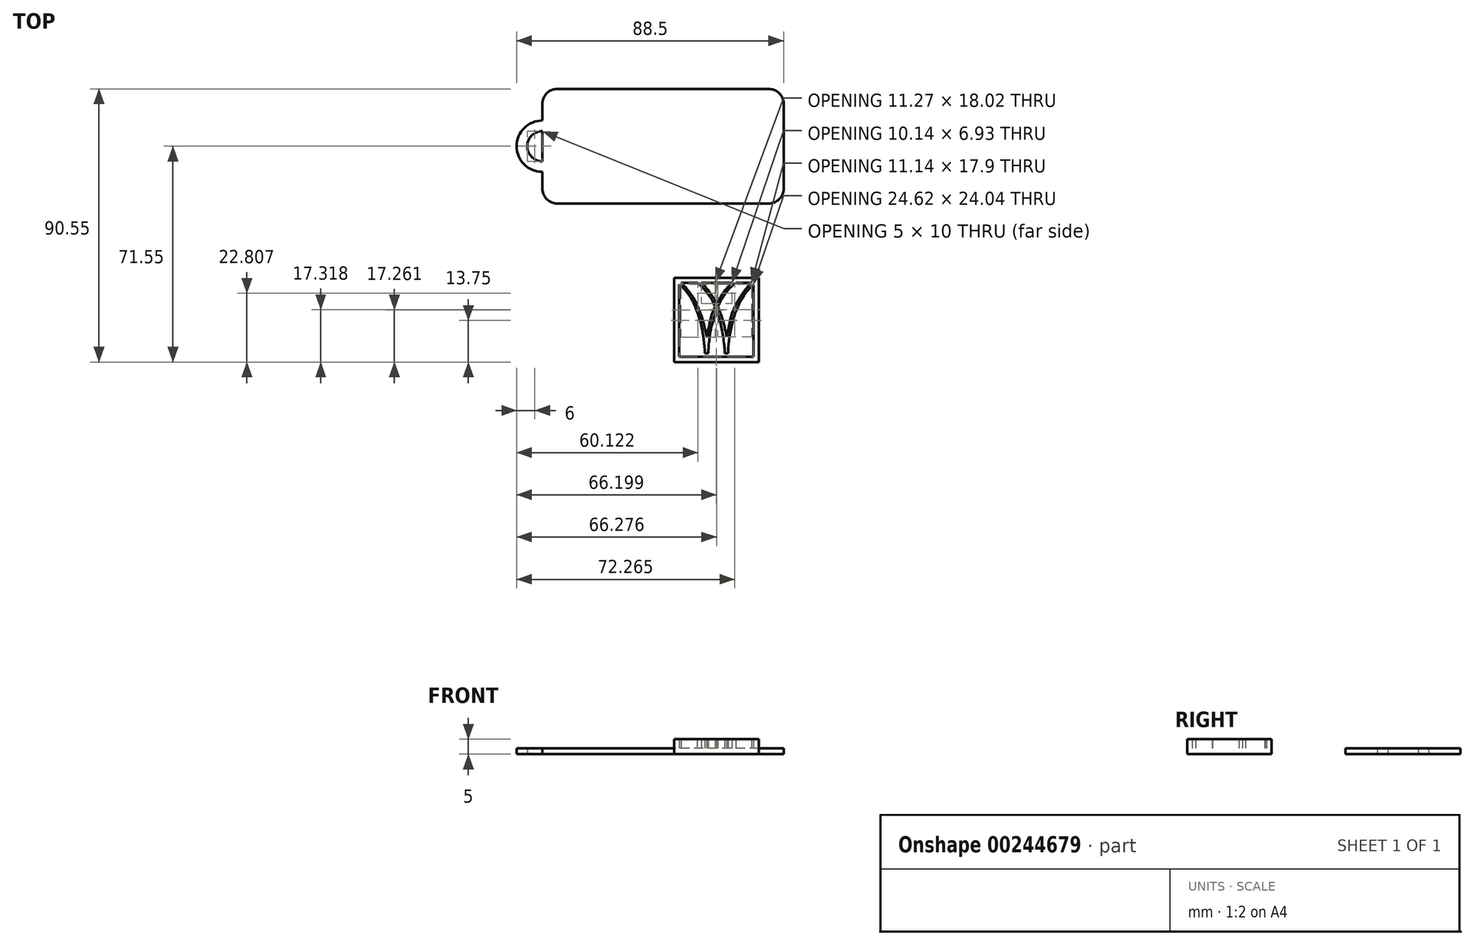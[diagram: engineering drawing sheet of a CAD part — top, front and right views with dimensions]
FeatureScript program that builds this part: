
annotation { "Feature Type Name" : "Feature", "Feature Type Description" : "" }
export const myFeature = defineFeature(function(context is Context, id is Id, definition is map)
    precondition{}
    {
        {
            var Q0;
            Q0=qCreatedBy(makeId("Top.planeOp"),FACE);
            var sketch = newSketch(context, id + "F0", { "sketchPlane" : qUnion([Q0])});
            skLineSegment(sketch, "E0.bottom", {"start": v(40, -19) * mm, "end": v(-40, -19) * mm});
            skLineSegment(sketch, "E0.top", {"start": v(40, 19) * mm, "end": v(-40, 19) * mm});
            skLineSegment(sketch, "E0.left", {"start": v(40, -19) * mm, "end": v(40, 19) * mm});
            skLineSegment(sketch, "E0.right", {"start": v(-40, -19) * mm, "end": v(-40, 19) * mm});
            skPoint(sketch, "E0.middle", {"position": v(0, 0) * mm});
            skArc(sketch, "E1", {"start": v(-40, 8.5) * mm, "mid": v(-48.5, 0) * mm, "end": v(-40, -8.5) * mm});
            skArc(sketch, "E2", {"start": v(-40, 5) * mm, "mid": v(-45, 0) * mm, "end": v(-40, -5) * mm});
            skLineSegment(sketch, "E3.bottom", {"start": v(3.67, -43.6) * mm, "end": v(31.76, -43.6) * mm});
            skLineSegment(sketch, "E3.top", {"start": v(3.67, -71.55) * mm, "end": v(31.76, -71.55) * mm});
            skLineSegment(sketch, "E3.left", {"start": v(3.67, -43.6) * mm, "end": v(3.67, -71.55) * mm});
            skLineSegment(sketch, "E3.right", {"start": v(31.76, -43.6) * mm, "end": v(31.76, -71.55) * mm});
            skLineSegment(sketch, "E4.bottom", {"start": v(30, -69.82) * mm, "end": v(5.4, -69.82) * mm});
            skLineSegment(sketch, "E4.top", {"start": v(30, -45.28) * mm, "end": v(5.4, -45.28) * mm});
            skLineSegment(sketch, "E4.left", {"start": v(30, -69.82) * mm, "end": v(30, -45.28) * mm});
            skLineSegment(sketch, "E4.right", {"start": v(5.4, -69.82) * mm, "end": v(5.4, -45.28) * mm});
            skFitSpline(sketch, "E5", {"points": [v(5.4, -45.78) * mm, v(6.95, -47.25) * mm, v(8.96, -49.9) * mm, v(10.75, -53.4) * mm, v(12.3, -57.85) * mm, v(12.92, -60.44) * mm, v(13.59, -64.66) * mm, v(13.88, -68.66) * mm], "startDerivative": vector(13.72, -12.02) * mm, "endDerivative": vector(1.24, -25.5) * mm});
            skLineSegment(sketch, "E6", {"start": v(13.88, -68.66) * mm, "end": v(15.03, -68.66) * mm});
            skFitSpline(sketch, "E7", {"points": [v(15.03, -68.66) * mm, v(15.2, -65.34) * mm, v(15.98, -60.4) * mm, v(16.73, -57.42) * mm, v(17.7, -54.42) * mm], "startDerivative": vector(0.33, 12.82) * mm, "endDerivative": vector(4.43, 13.1) * mm});
            skFitSpline(sketch, "E8", {"points": [v(17.7, -54.42) * mm, v(18.36, -56.17) * mm, v(19.16, -59.13) * mm, v(19.72, -61.75) * mm, v(20.15, -64.71) * mm, v(20.44, -67.34) * mm, v(20.48, -68.66) * mm], "startDerivative": vector(4.42, -10.88) * mm, "endDerivative": vector(0.05, -9.74) * mm});
            skLineSegment(sketch, "E9", {"start": v(20.48, -68.66) * mm, "end": v(21.59, -68.66) * mm});
            skFitSpline(sketch, "E10", {"points": [v(21.59, -68.66) * mm, v(21.7, -66.19) * mm, v(22.2, -62.35) * mm, v(23.04, -58.39) * mm, v(23.94, -55.4) * mm, v(25.1, -52.55) * mm, v(26.64, -49.72) * mm, v(28.46, -47.3) * mm, v(30, -45.87) * mm], "startDerivative": vector(0.58, 20.88) * mm, "endDerivative": vector(14.9, 12.68) * mm});
            skFitSpline(sketch, "E11", {"points": [v(17.7, -54.42) * mm, v(18.63, -52.27) * mm, v(20.21, -49.48) * mm, v(22, -47.16) * mm, v(24.12, -45.28) * mm], "startDerivative": vector(3.62, 9.1) * mm, "endDerivative": vector(8.76, 7.2) * mm});
            skFitSpline(sketch, "E12", {"points": [v(17.7, -54.42) * mm, v(16.5, -51.5) * mm, v(14.2, -48.03) * mm, v(12.54, -46.23) * mm, v(11.35, -45.28) * mm], "startDerivative": vector(-3.73, 10.52) * mm, "endDerivative": vector(-6.27, 4.74) * mm});
            skFitSpline(sketch, "E13", {"points": [v(5.99, -45.28) * mm, v(7.48, -46.75) * mm, v(10.14, -50.36) * mm, v(11.42, -52.95) * mm, v(12.6, -55.95) * mm, v(13.64, -59.46) * mm, v(14.5, -63.3) * mm], "startDerivative": vector(10.37, -9.34) * mm, "endDerivative": vector(4.52, -21.45) * mm});
            skFitSpline(sketch, "E14", {"points": [v(14.5, -63.3) * mm, v(14.8, -61.73) * mm, v(15.3, -59.46) * mm, v(15.98, -56.48) * mm, v(16.94, -53.86) * mm, v(18.43, -51.04) * mm, v(20.41, -47.98) * mm, v(22.24, -45.87) * mm, v(22.84, -45.28) * mm], "startDerivative": vector(2.57, 14.95) * mm, "endDerivative": vector(7.13, 6.69) * mm});
            skFitSpline(sketch, "E15", {"points": [v(12.7, -45.28) * mm, v(14.1, -46.64) * mm, v(16.76, -50.25) * mm, v(18.04, -52.83) * mm, v(19.21, -55.84) * mm, v(20.26, -59.34) * mm, v(21.12, -63.18) * mm], "startDerivative": vector(10.37, -9.34) * mm, "endDerivative": vector(4.52, -21.45) * mm});
            skFitSpline(sketch, "E16", {"points": [v(21.12, -63.18) * mm, v(21.4, -61.62) * mm, v(21.9, -59.34) * mm, v(22.6, -56.36) * mm, v(23.55, -53.75) * mm, v(25.04, -50.93) * mm, v(27.03, -47.87) * mm, v(28.86, -45.75) * mm, v(29.33, -45.28) * mm], "startDerivative": vector(2.57, 14.95) * mm, "endDerivative": vector(7.13, 6.69) * mm});
            skSolve(sketch);
        }
        {
            var Q0;
            {var subQ0=sQuery(id+"F0.wireOp",EDGE,"E1");Q0=makeQuery(id+"F0.imprint","IMPRINT",FACE,{"disambiguationData":[TD([[makeQuery(id+"F0.imprint","IMPRINT",EDGE,{"derivedFrom":subQ0}),1.0]])]});}
            var Q1;
            {var subQ1=sQuery(id+"F0.wireOp",EDGE,"E0.bottom");Q1=makeQuery(id+"F0.imprint","IMPRINT",FACE,{"disambiguationData":[TD([[makeQuery(id+"F0.imprint","IMPRINT",EDGE,{"derivedFrom":subQ1}),-1.0]])]});}
            extrude(context, id + "F1", {"entities" : qUnion([Q0, Q1]), "depth" : 2 * mm});
        }
        {
            var Q0;
            Q0=makeQuery(id+"F1.opExtrude","SWEPT_EDGE",EDGE,{"disambiguationData":[OSD([sQuery(id+"F0.wireOp",EDGE,"E0.top"),sQuery(id+"F0.wireOp",EDGE,"E0.right")])]});
            var Q1;
            Q1=makeQuery(id+"F1.opExtrude","SWEPT_EDGE",EDGE,{"disambiguationData":[OSD([sQuery(id+"F0.wireOp",EDGE,"E0.top"),sQuery(id+"F0.wireOp",EDGE,"E0.left")])]});
            var Q2;
            Q2=makeQuery(id+"F1.opExtrude","SWEPT_EDGE",EDGE,{"disambiguationData":[OSD([sQuery(id+"F0.wireOp",EDGE,"E0.bottom"),sQuery(id+"F0.wireOp",EDGE,"E0.right")])]});
            var Q3;
            Q3=makeQuery(id+"F1.opExtrude","SWEPT_EDGE",EDGE,{"disambiguationData":[OSD([sQuery(id+"F0.wireOp",EDGE,"E0.bottom"),sQuery(id+"F0.wireOp",EDGE,"E0.left")])]});
            fillet(context, id + "F2", {"entities" : qUnion([Q0, Q1, Q2, Q3]), "radius" : 5 * mm, "tangentPropagation" : true, "allowEdgeOverflow" : false});
        }
        {
            var Q0;
            Q0=makeQuery(id+"F0.imprint","IMPRINT",FACE,{"disambiguationData":[TD([[makeQuery(id+"F0.imprint","IMPRINT",EDGE,{"derivedFrom":sQuery(id+"F0.wireOp",EDGE,"E3.bottom")}),-1.0]])]});
            var Q1;
            {var subQ3=sQuery(id+"F0.wireOp",EDGE,"E5");Q1=makeQuery(id+"F0.imprint","IMPRINT",FACE,{"disambiguationData":[TD([[makeQuery(id+"F0.imprint","IMPRINT",EDGE,{"derivedFrom":subQ3}),1.0]])]});}
            var Q2;
            {var subQ0=sQuery(id+"F0.wireOp",EDGE,"E12");var subQ1=sQuery(id+"F0.wireOp",EDGE,"E4.top");var subQ2=makeQuery(id+"F0.imprint","INTERSECT",VERTEX,{"derivedFrom":[subQ1,subQ0]});Q2=makeQuery(id+"F0.imprint","IMPRINT",FACE,{"disambiguationData":[TD([[makeQuery(id+"F0.imprint","IMPRINT",EDGE,{"disambiguationData":[TD([[subQ2,1.0]])],"derivedFrom":subQ1}),1.0]])]});}
            var Q3;
            {var subQ0=sQuery(id+"F0.wireOp",EDGE,"E12");var subQ5=sQuery(id+"F0.wireOp",EDGE,"E14");var subQ6=makeQuery(id+"F0.imprint","INTERSECT",VERTEX,{"derivedFrom":[subQ0,subQ5]});Q3=makeQuery(id+"F0.imprint","IMPRINT",FACE,{"disambiguationData":[TD([[makeQuery(id+"F0.imprint","IMPRINT",EDGE,{"disambiguationData":[TD([[subQ6,-1.0]])],"derivedFrom":subQ5}),-1.0]])]});}
            var Q4;
            {var subQ0=sQuery(id+"F0.wireOp",EDGE,"E11");var subQ1=sQuery(id+"F0.wireOp",EDGE,"E4.top");var subQ2=makeQuery(id+"F0.imprint","INTERSECT",VERTEX,{"derivedFrom":[subQ1,subQ0]});Q4=makeQuery(id+"F0.imprint","IMPRINT",FACE,{"disambiguationData":[TD([[makeQuery(id+"F0.imprint","IMPRINT",EDGE,{"disambiguationData":[TD([[subQ2,-1.0]])],"derivedFrom":subQ1}),1.0]])]});}
            var Q5;
            {var subQ0=sQuery(id+"F0.wireOp",EDGE,"E8");Q5=makeQuery(id+"F0.imprint","IMPRINT",FACE,{"disambiguationData":[TD([[makeQuery(id+"F0.imprint","IMPRINT",EDGE,{"derivedFrom":subQ0}),1.0]])]});}
            extrude(context, id + "F3", {"entities" : qUnion([Q0, Q1, Q2, Q3, Q4, Q5]), "depth" : 5 * mm});
        }
        {
            var Q0;
            Q0=makeQuery(id+"F3.opExtrude","SWEPT_FACE",FACE,{"disambiguationData":[OSD([sQuery(id+"F0.wireOp",EDGE,"E3.right")])]});
            var sketch = newSketch(context, id + "F4", { "sketchPlane" : qUnion([Q0])});
            skLineSegment(sketch, "E17", {"start": v(-63.16, 5) * mm, "end": v(-63.16, 0) * mm});
            skLineSegment(sketch, "E18", {"start": v(-63.16, 0) * mm, "end": v(-43.6, 0) * mm});
            skLineSegment(sketch, "E19", {"start": v(-43.6, 0) * mm, "end": v(-63.16, 5) * mm});
            skSolve(sketch);
        }
        {
            var Q0;
            Q0=makeQuery(id+"F4.imprint","IMPRINT",FACE,{"disambiguationData":[TD([[makeQuery(id+"F4.imprint","IMPRINT",EDGE,{"derivedFrom":sQuery(id+"F4.wireOp",EDGE,"E17")}),1.0]])]});
            extrude(context, id + "F5", {"entities" : qUnion([Q0]), "oppositeDirection" : true, "depth" : 27.05 * mm});
        }
        {
            var Q0;
            Q0=makeQuery(id+"F3.opExtrude","SWEPT_BODY",BODY,{"disambiguationData":[OSD([sQuery(id+"F0.wireOp",EDGE,"E3.bottom"),sQuery(id+"F0.wireOp",EDGE,"E3.top"),sQuery(id+"F0.wireOp",EDGE,"E3.left"),sQuery(id+"F0.wireOp",EDGE,"E3.right"),sQuery(id+"F0.wireOp",EDGE,"E4.bottom"),sQuery(id+"F0.wireOp",EDGE,"E4.top"),sQuery(id+"F0.wireOp",EDGE,"E4.left"),sQuery(id+"F0.wireOp",EDGE,"E4.right"),sQuery(id+"F0.wireOp",EDGE,"E5"),sQuery(id+"F0.wireOp",EDGE,"E6"),sQuery(id+"F0.wireOp",EDGE,"E7"),sQuery(id+"F0.wireOp",EDGE,"E8"),sQuery(id+"F0.wireOp",EDGE,"E9"),sQuery(id+"F0.wireOp",EDGE,"E10"),sQuery(id+"F0.wireOp",EDGE,"E11"),sQuery(id+"F0.wireOp",EDGE,"E12"),sQuery(id+"F0.wireOp",EDGE,"E13"),sQuery(id+"F0.wireOp",EDGE,"E14"),sQuery(id+"F0.wireOp",EDGE,"E15"),sQuery(id+"F0.wireOp",EDGE,"E16")])]});
            var Q1;
            Q1=makeQuery(id+"F5.opExtrude","SWEPT_BODY",BODY,{"disambiguationData":[OSD([sQuery(id+"F4.wireOp",EDGE,"E17"),sQuery(id+"F4.wireOp",EDGE,"E18"),sQuery(id+"F4.wireOp",EDGE,"E19")])]});
            booleanBodies(context, id + "F6", {"operationType" : BooleanOperationType.SUBTRACTION, "tools" : qUnion([Q0]), "targets" : qUnion([Q1]), "keepTools" : true});
        }
        {
            var Q0;
            Q0=makeQuery(id+"F6.opBoolean","SPLIT",BODY,{"disambiguationData":[OD(4.0)],"derivedFrom":makeQuery(id+"F5.opExtrude","SWEPT_BODY",BODY,{"disambiguationData":[OSD([sQuery(id+"F4.wireOp",EDGE,"E17"),sQuery(id+"F4.wireOp",EDGE,"E18"),sQuery(id+"F4.wireOp",EDGE,"E19")])]})});
            var Q1;
            Q1=makeQuery(id+"F6.opBoolean","SPLIT",BODY,{"disambiguationData":[OD(5.0)],"derivedFrom":makeQuery(id+"F5.opExtrude","SWEPT_BODY",BODY,{"disambiguationData":[OSD([sQuery(id+"F4.wireOp",EDGE,"E17"),sQuery(id+"F4.wireOp",EDGE,"E18"),sQuery(id+"F4.wireOp",EDGE,"E19")])]})});
            var Q2;
            Q2=makeQuery(id+"F6.opBoolean","SPLIT",BODY,{"disambiguationData":[OD(3.0)],"derivedFrom":makeQuery(id+"F5.opExtrude","SWEPT_BODY",BODY,{"disambiguationData":[OSD([sQuery(id+"F4.wireOp",EDGE,"E17"),sQuery(id+"F4.wireOp",EDGE,"E18"),sQuery(id+"F4.wireOp",EDGE,"E19")])]})});
            deleteBodies(context, id + "F7", {"entities" : qUnion([Q0, Q1, Q2])});
        }
    });
